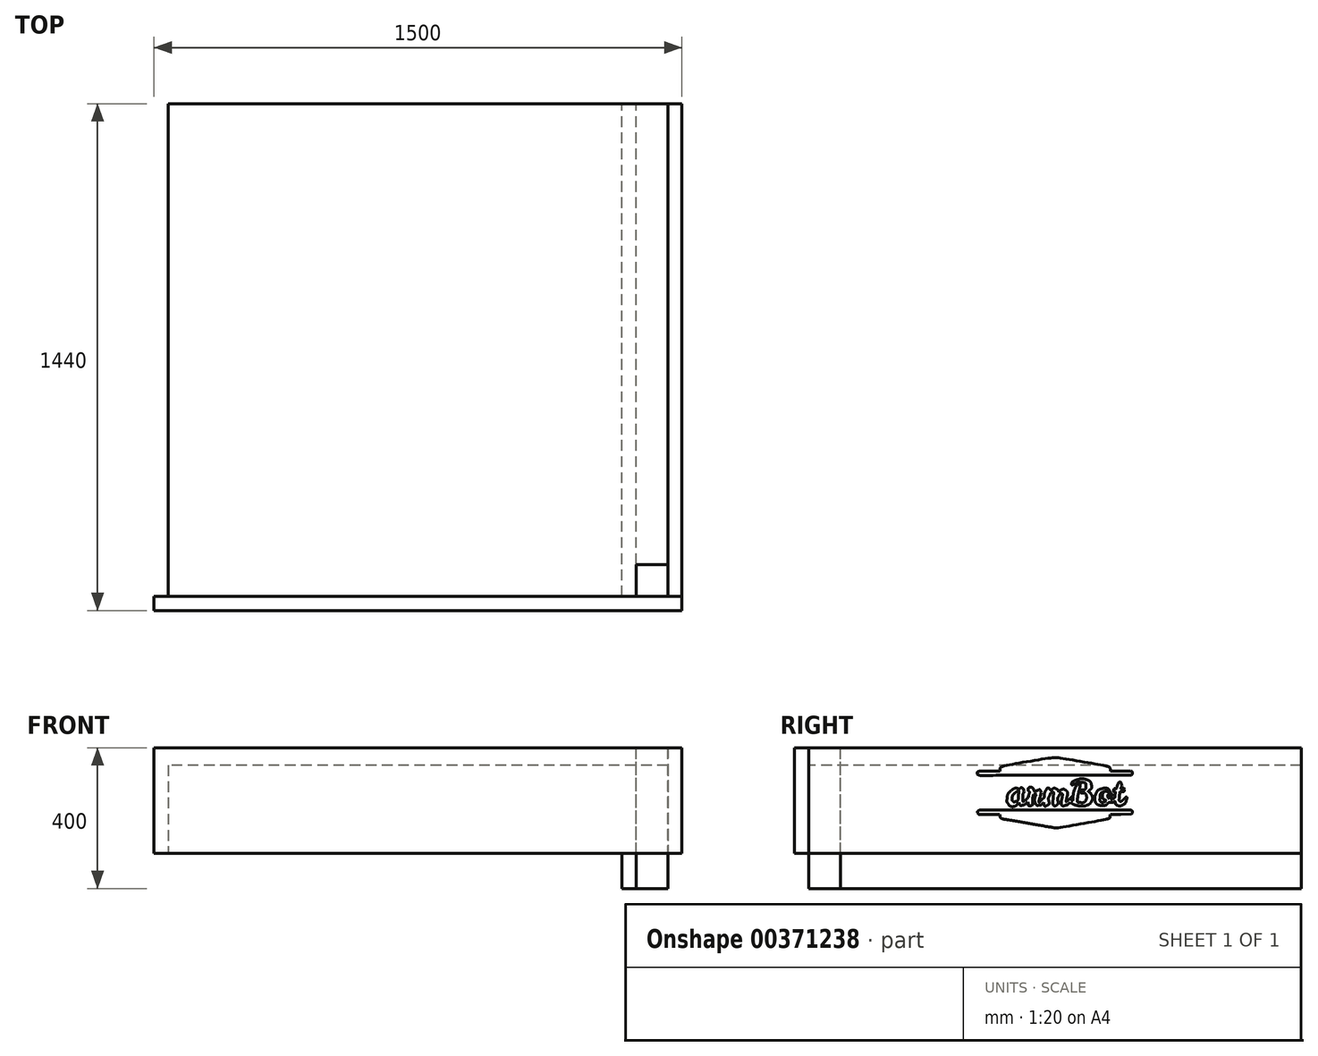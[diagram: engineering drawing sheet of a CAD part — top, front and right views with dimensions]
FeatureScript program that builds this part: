
annotation { "Feature Type Name" : "Feature", "Feature Type Description" : "" }
export const myFeature = defineFeature(function(context is Context, id is Id, definition is map)
    precondition{}
    {
        {
            var Q0;
            Q0=qCreatedBy(makeId("Top.planeOp"),FACE);
            var sketch = newSketch(context, id + "F0", { "sketchPlane" : qUnion([Q0])});
            skLineSegment(sketch, "E0.bottom", {"start": v(710, 700) * mm, "end": v(-710, 700) * mm});
            skLineSegment(sketch, "E0.top", {"start": v(710, -700) * mm, "end": v(-710, -700) * mm});
            skLineSegment(sketch, "E0.left", {"start": v(710, 700) * mm, "end": v(710, -700) * mm});
            skLineSegment(sketch, "E0.right", {"start": v(-710, 700) * mm, "end": v(-710, -700) * mm});
            skPoint(sketch, "E0.middle", {"position": v(0, 0) * mm});
            skSolve(sketch);
        }
        {
            var Q0;
            Q0 = qSketchRegion(id + "F0", true);
            extrude(context, id + "F1", {"entities" : qUnion([Q0]), "depth" : 250 * mm});
        }
        {
            var Q0;
            Q0=makeQuery(id+"F1.opExtrude","SWEPT_FACE",FACE,{"disambiguationData":[OSD([sQuery(id+"F0.wireOp",EDGE,"E0.left")])]});
            var sketch = newSketch(context, id + "F2", { "sketchPlane" : qUnion([Q0])});
            skLineSegment(sketch, "E1.bottom", {"start": v(-700, 0) * mm, "end": v(700, 0) * mm});
            skLineSegment(sketch, "E1.top", {"start": v(-700, 300) * mm, "end": v(700, 300) * mm});
            skLineSegment(sketch, "E1.left", {"start": v(-700, 0) * mm, "end": v(-700, 300) * mm});
            skLineSegment(sketch, "E1.right", {"start": v(700, 0) * mm, "end": v(700, 300) * mm});
            skSolve(sketch);
        }
        {
            var Q0;
            Q0=qSketchRegion(id+"F2",true);
            extrude(context, id + "F3", {"entities" : qUnion([Q0]), "depth" : 40 * mm});
        }
        {
            var Q0;
            Q0=makeQuery(id+"F1.opExtrude","SWEPT_FACE",FACE,{"disambiguationData":[OSD([sQuery(id+"F0.wireOp",EDGE,"E0.top")])]});
            var sketch = newSketch(context, id + "F4", { "sketchPlane" : qUnion([Q0])});
            skLineSegment(sketch, "E2.bottom", {"start": v(-750, 300) * mm, "end": v(750, 300) * mm});
            skLineSegment(sketch, "E2.top", {"start": v(-750, 0) * mm, "end": v(750, 0) * mm});
            skLineSegment(sketch, "E2.left", {"start": v(-750, 300) * mm, "end": v(-750, 0) * mm});
            skLineSegment(sketch, "E2.right", {"start": v(750, 300) * mm, "end": v(750, 0) * mm});
            skSolve(sketch);
        }
        {
            var Q0;
            Q0=qSketchRegion(id+"F4",true);
            extrude(context, id + "F5", {"entities" : qUnion([Q0]), "depth" : 40 * mm});
        }
        {
            var Q0;
            Q0=makeQuery(id+"F1.opExtrude","CAP_FACE",FACE,{"disambiguationData":[OSD([sQuery(id+"F0.wireOp",EDGE,"E0.bottom"),sQuery(id+"F0.wireOp",EDGE,"E0.top"),sQuery(id+"F0.wireOp",EDGE,"E0.left"),sQuery(id+"F0.wireOp",EDGE,"E0.right")])],"isStart":false});
            var sketch = newSketch(context, id + "F6", { "sketchPlane" : qUnion([Q0])});
            skFitSpline(sketch, "E3", {"points": [v(-9.76, -247.93) * mm, v(-14.36, -247) * mm, v(-98.7, -232.48) * mm, v(-197.18, -215.67) * mm]});
            skFitSpline(sketch, "E4", {"points": [v(-197.18, -215.67) * mm, v(-303.5, -197.52) * mm, v(-377.79, -184.02) * mm, v(-380.05, -182.43) * mm]});
            skFitSpline(sketch, "E5", {"points": [v(-380.05, -182.43) * mm, v(-386.35, -178.01) * mm, v(-389.22, -172.54) * mm, v(-390.38, -162.7) * mm]});
            skLineSegment(sketch, "E6", {"start": v(-390.38, -162.7) * mm, "end": v(-391.49, -153.38) * mm});
            skLineSegment(sketch, "E7", {"start": v(-391.49, -153.38) * mm, "end": v(-463.29, -153.35) * mm});
            skFitSpline(sketch, "E8", {"points": [v(-463.29, -153.35) * mm, v(-540.74, -153.32) * mm, v(-542.21, -153.15) * mm, v(-546.84, -143.5) * mm]});
            skFitSpline(sketch, "E9", {"points": [v(-546.84, -143.5) * mm, v(-550.32, -136.23) * mm, v(-547.5, -129.03) * mm, v(-539.62, -125.02) * mm]});
            skFitSpline(sketch, "E10", {"points": [v(-539.62, -125.02) * mm, v(-533.58, -121.95) * mm, v(-503.94, -121.77) * mm, v(0.65, -121.77) * mm]});
            skFitSpline(sketch, "E11", {"points": [v(0.65, -121.77) * mm, v(385.66, -121.76) * mm, v(536.18, -122.34) * mm, v(540.43, -123.82) * mm]});
            skFitSpline(sketch, "E12", {"points": [v(540.43, -123.82) * mm, v(543.67, -124.95) * mm, v(547.14, -127.4) * mm, v(548.14, -129.27) * mm]});
            skFitSpline(sketch, "E13", {"points": [v(548.14, -129.27) * mm, v(551.05, -134.7) * mm, v(550.26, -143.3) * mm, v(546.41, -148.06) * mm]});
            skLineSegment(sketch, "E14", {"start": v(546.41, -148.06) * mm, "end": v(542.86, -152.45) * mm});
            skLineSegment(sketch, "E15", {"start": v(542.86, -152.45) * mm, "end": v(467.85, -153.38) * mm});
            skLineSegment(sketch, "E16", {"start": v(467.85, -153.38) * mm, "end": v(392.83, -154.3) * mm});
            skLineSegment(sketch, "E17", {"start": v(392.83, -154.3) * mm, "end": v(392.5, -162.05) * mm});
            skFitSpline(sketch, "E18", {"points": [v(392.5, -162.05) * mm, v(391.99, -173.78) * mm, v(387.68, -180.46) * mm, v(378.46, -183.85) * mm]});
            skFitSpline(sketch, "E19", {"points": [v(378.46, -183.85) * mm, v(371.97, -186.24) * mm, v(2.57, -250.58) * mm, v(-0.47, -249.85) * mm]});
            skFitSpline(sketch, "E20", {"points": [v(-0.47, -249.85) * mm, v(-0.98, -249.73) * mm, v(-5.16, -248.87) * mm, v(-9.76, -247.93) * mm]});
            skLineSegment(sketch, "E21", {"start": v(-9.76, -247.93) * mm, "end": v(-9.76, -247.93) * mm});
            skFitSpline(sketch, "E22", {"points": [v(163.18, -91.34) * mm, v(144.56, -86.99) * mm, v(127.82, -80.58) * mm, v(118.25, -74.15) * mm]});
            skLineSegment(sketch, "E23", {"start": v(118.25, -74.15) * mm, "end": v(108.82, -67.8) * mm});
            skLineSegment(sketch, "E24", {"start": v(108.82, -67.8) * mm, "end": v(101.7, -74.22) * mm});
            skFitSpline(sketch, "E25", {"points": [v(101.7, -74.22) * mm, v(92.92, -82.15) * mm, v(86.06, -85.78) * mm, v(75.22, -88.2) * mm]});
            skFitSpline(sketch, "E26", {"points": [v(75.22, -88.2) * mm, v(52.86, -93.22) * mm, v(44.33, -75.76) * mm, v(50.52, -37.64) * mm]});
            skFitSpline(sketch, "E27", {"points": [v(50.52, -37.64) * mm, v(54.63, -12.34) * mm, v(54.44, -8.7) * mm, v(48.9, -6.17) * mm]});
            skFitSpline(sketch, "E28", {"points": [v(48.9, -6.17) * mm, v(42.7, -3.35) * mm, v(36.64, -7.44) * mm, v(29.87, -18.99) * mm]});
            skFitSpline(sketch, "E29", {"points": [v(29.87, -18.99) * mm, v(21.01, -34.1) * mm, v(18.43, -44.15) * mm, v(20.53, -55.3) * mm]});
            skFitSpline(sketch, "E30", {"points": [v(20.53, -55.3) * mm, v(21.54, -60.66) * mm, v(22.46, -68.35) * mm, v(22.57, -72.38) * mm]});
            skFitSpline(sketch, "E31", {"points": [v(22.57, -72.38) * mm, v(22.76, -78.97) * mm, v(22, -80.26) * mm, v(14.95, -85.23) * mm]});
            skFitSpline(sketch, "E32", {"points": [v(14.95, -85.23) * mm, v(4.39, -92.68) * mm, v(-7.54, -93.24) * mm, v(-11.04, -86.43) * mm]});
            skFitSpline(sketch, "E33", {"points": [v(-11.04, -86.43) * mm, v(-13.95, -80.76) * mm, v(-14.16, -56.28) * mm, v(-11.54, -26.93) * mm]});
            skFitSpline(sketch, "E34", {"points": [v(-11.54, -26.93) * mm, v(-9.2, -0.66) * mm, v(-9.84, 2.83) * mm, v(-17.07, 2.83) * mm]});
            skFitSpline(sketch, "E35", {"points": [v(-17.07, 2.83) * mm, v(-23.9, 2.83) * mm, v(-30.46, -4.7) * mm, v(-38.87, -22.23) * mm]});
            skFitSpline(sketch, "E36", {"points": [v(-38.87, -22.23) * mm, v(-45.93, -36.93) * mm, v(-46.62, -45.33) * mm, v(-42.27, -63.77) * mm]});
            skFitSpline(sketch, "E37", {"points": [v(-42.27, -63.77) * mm, v(-38.91, -78.01) * mm, v(-39.9, -80.3) * mm, v(-52.19, -87) * mm]});
            skFitSpline(sketch, "E38", {"points": [v(-52.19, -87) * mm, v(-68.26, -95.75) * mm, v(-75.2, -92.86) * mm, v(-77.56, -76.43) * mm]});
            skLineSegment(sketch, "E39", {"start": v(-77.56, -76.43) * mm, "end": v(-78.86, -67.36) * mm});
            skLineSegment(sketch, "E40", {"start": v(-78.86, -67.36) * mm, "end": v(-86.62, -74.83) * mm});
            skFitSpline(sketch, "E41", {"points": [v(-86.62, -74.83) * mm, v(-97.05, -84.9) * mm, v(-104.92, -88.54) * mm, v(-116.78, -88.82) * mm]});
            skFitSpline(sketch, "E42", {"points": [v(-116.78, -88.82) * mm, v(-128.34, -89.1) * mm, v(-132.94, -86) * mm, v(-138.3, -74.35) * mm]});
            skFitSpline(sketch, "E43", {"points": [v(-138.3, -74.35) * mm, v(-144.12, -61.65) * mm, v(-141.58, -31.54) * mm, v(-133.32, -15.58) * mm]});
            skLineSegment(sketch, "E44", {"start": v(-133.32, -15.58) * mm, "end": v(-130.44, -10) * mm});
            skLineSegment(sketch, "E45", {"start": v(-130.44, -10) * mm, "end": v(-141.2, -10.56) * mm});
            skLineSegment(sketch, "E46", {"start": v(-141.2, -10.56) * mm, "end": v(-151.94, -11.12) * mm});
            skLineSegment(sketch, "E47", {"start": v(-151.94, -11.12) * mm, "end": v(-155.34, -25.07) * mm});
            skFitSpline(sketch, "E48", {"points": [v(-155.34, -25.07) * mm, v(-157.97, -35.9) * mm, v(-158.52, -43.56) * mm, v(-157.8, -59.34) * mm]});
            skFitSpline(sketch, "E49", {"points": [v(-157.8, -59.34) * mm, v(-157.29, -70.85) * mm, v(-157.67, -81.12) * mm, v(-158.7, -83.03) * mm]});
            skFitSpline(sketch, "E50", {"points": [v(-158.7, -83.03) * mm, v(-161.25, -87.81) * mm, v(-170.24, -92.01) * mm, v(-177.92, -92.01) * mm]});
            skFitSpline(sketch, "E51", {"points": [v(-177.92, -92.01) * mm, v(-186.08, -92.01) * mm, v(-189.42, -87.45) * mm, v(-191.2, -73.87) * mm]});
            skLineSegment(sketch, "E52", {"start": v(-191.2, -73.87) * mm, "end": v(-192.48, -64.09) * mm});
            skLineSegment(sketch, "E53", {"start": v(-192.48, -64.09) * mm, "end": v(-200.42, -71.4) * mm});
            skFitSpline(sketch, "E54", {"points": [v(-200.42, -71.4) * mm, v(-209.89, -80.13) * mm, v(-220.17, -85.65) * mm, v(-231.87, -88.27) * mm]});
            skFitSpline(sketch, "E55", {"points": [v(-231.87, -88.27) * mm, v(-243.7, -90.92) * mm, v(-250.08, -87.49) * mm, v(-254.4, -76.16) * mm]});
            skLineSegment(sketch, "E56", {"start": v(-254.4, -76.16) * mm, "end": v(-257.65, -67.68) * mm});
            skLineSegment(sketch, "E57", {"start": v(-257.65, -67.68) * mm, "end": v(-262.94, -74.1) * mm});
            skFitSpline(sketch, "E58", {"points": [v(-262.94, -74.1) * mm, v(-279.38, -94.04) * mm, v(-316.37, -95.84) * mm, v(-331.85, -77.45) * mm]});
            skFitSpline(sketch, "E59", {"points": [v(-331.85, -77.45) * mm, v(-339.17, -68.75) * mm, v(-341.42, -59.86) * mm, v(-340.14, -44.75) * mm]});
            skFitSpline(sketch, "E60", {"points": [v(-340.14, -44.75) * mm, v(-338.13, -20.94) * mm, v(-329.14, -1.86) * mm, v(-313.1, 12.61) * mm]});
            skFitSpline(sketch, "E61", {"points": [v(-313.1, 12.61) * mm, v(-297.94, 26.32) * mm, v(-276.95, 32.69) * mm, v(-259.7, 28.82) * mm]});
            skFitSpline(sketch, "E62", {"points": [v(-259.7, 28.82) * mm, v(-252.55, 27.22) * mm, v(-250.45, 27.38) * mm, v(-247.85, 29.73) * mm]});
            skFitSpline(sketch, "E63", {"points": [v(-247.85, 29.73) * mm, v(-240.93, 36) * mm, v(-226.99, 30.32) * mm, v(-220.73, 18.7) * mm]});
            skLineSegment(sketch, "E64", {"start": v(-220.73, 18.7) * mm, "end": v(-217.21, 12.17) * mm});
            skLineSegment(sketch, "E65", {"start": v(-217.21, 12.17) * mm, "end": v(-223.2, 0.02) * mm});
            skFitSpline(sketch, "E66", {"points": [v(-223.2, 0.02) * mm, v(-228.92, -11.58) * mm, v(-229.19, -13.1) * mm, v(-229.16, -33.94) * mm]});
            skFitSpline(sketch, "E67", {"points": [v(-229.16, -33.94) * mm, v(-229.13, -57.9) * mm, v(-228.1, -61.48) * mm, v(-221.81, -59.49) * mm]});
            skFitSpline(sketch, "E68", {"points": [v(-221.81, -59.49) * mm, v(-215.07, -57.35) * mm, v(-188.28, -30.28) * mm, v(-188.28, -25.6) * mm]});
            skFitSpline(sketch, "E69", {"points": [v(-188.28, -25.6) * mm, v(-188.28, -23.36) * mm, v(-186.22, -15.85) * mm, v(-183.7, -8.92) * mm]});
            skFitSpline(sketch, "E70", {"points": [v(-183.7, -8.92) * mm, v(-179.26, 3.33) * mm, v(-179.23, 3.78) * mm, v(-182.54, 7.44) * mm]});
            skFitSpline(sketch, "E71", {"points": [v(-182.54, 7.44) * mm, v(-188.48, 13.98) * mm, v(-190.53, 19.67) * mm, v(-189.3, 26.21) * mm]});
            skFitSpline(sketch, "E72", {"points": [v(-189.3, 26.21) * mm, v(-187.82, 34.15) * mm, v(-182.12, 38.16) * mm, v(-172.31, 38.16) * mm]});
            skFitSpline(sketch, "E73", {"points": [v(-172.31, 38.16) * mm, v(-163.16, 38.16) * mm, v(-156.23, 32.34) * mm, v(-150.73, 20.03) * mm]});
            skFitSpline(sketch, "E74", {"points": [v(-150.73, 20.03) * mm, v(-147.7, 13.24) * mm, v(-146.4, 12.12) * mm, v(-141.55, 12.12) * mm]});
            skFitSpline(sketch, "E75", {"points": [v(-141.55, 12.12) * mm, v(-138.45, 12.12) * mm, v(-130.4, 14.33) * mm, v(-123.66, 17.03) * mm]});
            skFitSpline(sketch, "E76", {"points": [v(-123.66, 17.03) * mm, v(-109.3, 22.78) * mm, v(-107.41, 22.17) * mm, v(-101.2, 9.8) * mm]});
            skLineSegment(sketch, "E77", {"start": v(-101.2, 9.8) * mm, "end": v(-96.87, 1.18) * mm});
            skLineSegment(sketch, "E78", {"start": v(-96.87, 1.18) * mm, "end": v(-104.6, -26.95) * mm});
            skFitSpline(sketch, "E79", {"points": [v(-104.6, -26.95) * mm, v(-115.26, -65.72) * mm, v(-113.52, -68.38) * mm, v(-91.12, -47.46) * mm]});
            skLineSegment(sketch, "E80", {"start": v(-91.12, -47.46) * mm, "end": v(-77.26, -34.51) * mm});
            skLineSegment(sketch, "E81", {"start": v(-77.26, -34.51) * mm, "end": v(-76.15, -22.7) * mm});
            skFitSpline(sketch, "E82", {"points": [v(-76.15, -22.7) * mm, v(-74.76, -7.77) * mm, v(-68.68, 10.87) * mm, v(-61.04, 23.61) * mm]});
            skFitSpline(sketch, "E83", {"points": [v(-61.04, 23.61) * mm, v(-56.21, 31.68) * mm, v(-54.07, 33.61) * mm, v(-49.45, 34.07) * mm]});
            skFitSpline(sketch, "E84", {"points": [v(-49.45, 34.07) * mm, v(-44.95, 34.52) * mm, v(-42.63, 33.32) * mm, v(-38.15, 28.2) * mm]});
            skFitSpline(sketch, "E85", {"points": [v(-38.15, 28.2) * mm, v(-35.04, 24.67) * mm, v(-32.16, 20.74) * mm, v(-31.73, 19.46) * mm]});
            skFitSpline(sketch, "E86", {"points": [v(-31.73, 19.46) * mm, v(-31.21, 17.9) * mm, v(-28.37, 19.02) * mm, v(-23, 22.9) * mm]});
            skFitSpline(sketch, "E87", {"points": [v(-23, 22.9) * mm, v(-11.96, 30.9) * mm, v(-1.17, 32.3) * mm, v(9.54, 27.1) * mm]});
            skFitSpline(sketch, "E88", {"points": [v(9.54, 27.1) * mm, v(18.23, 22.9) * mm, v(22.7, 17.7) * mm, v(24.79, 9.4) * mm]});
            skLineSegment(sketch, "E89", {"start": v(24.79, 9.4) * mm, "end": v(26.04, 4.44) * mm});
            skLineSegment(sketch, "E90", {"start": v(26.04, 4.44) * mm, "end": v(30.92, 9.1) * mm});
            skFitSpline(sketch, "E91", {"points": [v(30.92, 9.1) * mm, v(43.6, 21.22) * mm, v(66.06, 25.1) * mm, v(77.8, 17.18) * mm]});
            skFitSpline(sketch, "E92", {"points": [v(77.8, 17.18) * mm, v(81.26, 14.85) * mm, v(85.14, 10.88) * mm, v(86.42, 8.35) * mm]});
            skFitSpline(sketch, "E93", {"points": [v(86.42, 8.35) * mm, v(90.04, 1.18) * mm, v(89.21, -14.95) * mm, v(84.14, -35.88) * mm]});
            skFitSpline(sketch, "E94", {"points": [v(84.14, -35.88) * mm, v(81.59, -46.43) * mm, v(79.5, -56.26) * mm, v(79.5, -57.73) * mm]});
            skFitSpline(sketch, "E95", {"points": [v(79.5, -57.73) * mm, v(79.5, -63.6) * mm, v(86.26, -59.69) * mm, v(100.97, -45.33) * mm]});
            skFitSpline(sketch, "E96", {"points": [v(100.97, -45.33) * mm, v(110.63, -35.9) * mm, v(117.25, -30.77) * mm, v(118.65, -31.64) * mm]});
            skFitSpline(sketch, "E97", {"points": [v(118.65, -31.64) * mm, v(120.17, -32.58) * mm, v(120.56, -36.5) * mm, v(119.89, -43.92) * mm]});
            skFitSpline(sketch, "E98", {"points": [v(119.89, -43.92) * mm, v(118.95, -54.29) * mm, v(119.1, -54.82) * mm, v(123.1, -54.82) * mm]});
            skFitSpline(sketch, "E99", {"points": [v(123.1, -54.82) * mm, v(127.02, -54.82) * mm, v(127.36, -53.84) * mm, v(128.4, -39.48) * mm]});
            skFitSpline(sketch, "E100", {"points": [v(128.4, -39.48) * mm, v(130.72, -7.09) * mm, v(148.03, 43.77) * mm, v(160.6, 55.09) * mm]});
            skFitSpline(sketch, "E101", {"points": [v(160.6, 55.09) * mm, v(178.01, 70.78) * mm, v(179.9, 58.14) * mm, v(168.42, 2.83) * mm]});
            skFitSpline(sketch, "E102", {"points": [v(168.42, 2.83) * mm, v(163.73, -19.8) * mm, v(158.67, -63.5) * mm, v(160.5, -65.68) * mm]});
            skFitSpline(sketch, "E103", {"points": [v(160.5, -65.68) * mm, v(161.76, -67.18) * mm, v(175.96, -69.61) * mm, v(183.63, -69.64) * mm]});
            skFitSpline(sketch, "E104", {"points": [v(183.63, -69.64) * mm, v(200.98, -69.71) * mm, v(215.69, -61.64) * mm, v(220.83, -49.22) * mm]});
            skFitSpline(sketch, "E105", {"points": [v(220.83, -49.22) * mm, v(224.51, -40.34) * mm, v(222.43, -16.02) * mm, v(217.28, -7.68) * mm]});
            skFitSpline(sketch, "E106", {"points": [v(217.28, -7.68) * mm, v(213.13, -0.96) * mm, v(212.95, -0.9) * mm, v(200.63, -0.9) * mm]});
            skFitSpline(sketch, "E107", {"points": [v(200.63, -0.9) * mm, v(187.27, -0.9) * mm, v(181.1, 1.8) * mm, v(179.39, 8.35) * mm]});
            skFitSpline(sketch, "E108", {"points": [v(179.39, 8.35) * mm, v(178.82, 10.5) * mm, v(179.82, 13.89) * mm, v(181.7, 16.2) * mm]});
            skFitSpline(sketch, "E109", {"points": [v(181.7, 16.2) * mm, v(184.4, 19.56) * mm, v(187.56, 20.46) * mm, v(199.63, 21.31) * mm]});
            skFitSpline(sketch, "E110", {"points": [v(199.63, 21.31) * mm, v(213.63, 22.3) * mm, v(214.4, 22.6) * mm, v(217.02, 27.93) * mm]});
            skFitSpline(sketch, "E111", {"points": [v(217.02, 27.93) * mm, v(218.53, 31) * mm, v(219.77, 38.53) * mm, v(219.78, 44.67) * mm]});
            skFitSpline(sketch, "E112", {"points": [v(219.78, 44.67) * mm, v(219.8, 64.17) * mm, v(211.17, 71.67) * mm, v(187.07, 73.1) * mm]});
            skFitSpline(sketch, "E113", {"points": [v(187.07, 73.1) * mm, v(170.05, 74.11) * mm, v(157.7, 71.45) * mm, v(139.99, 62.97) * mm]});
            skFitSpline(sketch, "E114", {"points": [v(139.99, 62.97) * mm, v(124.82, 55.7) * mm, v(118.55, 54.98) * mm, v(118.55, 60.51) * mm]});
            skFitSpline(sketch, "E115", {"points": [v(118.55, 60.51) * mm, v(118.55, 70.5) * mm, v(143.11, 88.38) * mm, v(165.9, 94.95) * mm]});
            skFitSpline(sketch, "E116", {"points": [v(165.9, 94.95) * mm, v(181.16, 99.36) * mm, v(211.58, 97.92) * mm, v(227.33, 92.04) * mm]});
            skFitSpline(sketch, "E117", {"points": [v(227.33, 92.04) * mm, v(241.91, 86.6) * mm, v(254.67, 73.92) * mm, v(257.71, 61.83) * mm]});
            skFitSpline(sketch, "E118", {"points": [v(257.71, 61.83) * mm, v(262.48, 42.9) * mm, v(259.33, 31.38) * mm, v(245.79, 18.17) * mm]});
            skFitSpline(sketch, "E119", {"points": [v(245.79, 18.17) * mm, v(240.28, 12.8) * mm, v(236.48, 8.4) * mm, v(237.34, 8.4) * mm]});
            skFitSpline(sketch, "E120", {"points": [v(237.34, 8.4) * mm, v(241.01, 8.4) * mm, v(256.17, -7.19) * mm, v(259.81, -14.71) * mm]});
            skFitSpline(sketch, "E121", {"points": [v(259.81, -14.71) * mm, v(265.46, -26.39) * mm, v(265.68, -49.04) * mm, v(260.25, -59.68) * mm]});
            skFitSpline(sketch, "E122", {"points": [v(260.25, -59.68) * mm, v(254.38, -71.16) * mm, v(239.5, -83.55) * mm, v(225.92, -88.28) * mm]});
            skFitSpline(sketch, "E123", {"points": [v(225.92, -88.28) * mm, v(211.44, -93.33) * mm, v(178.53, -94.93) * mm, v(163.18, -91.34) * mm]});
            skFitSpline(sketch, "E124", {"points": [v(-281.84, -62.14) * mm, v(-267.85, -56.85) * mm, v(-259.05, -41.8) * mm, v(-258.98, -23.08) * mm]});
            skFitSpline(sketch, "E125", {"points": [v(-258.98, -23.08) * mm, v(-258.96, -16.37) * mm, v(-258.05, -6.04) * mm, v(-256.95, -0.12) * mm]});
            skFitSpline(sketch, "E126", {"points": [v(-256.95, -0.12) * mm, v(-255.86, 5.8) * mm, v(-255.42, 11.09) * mm, v(-255.98, 11.64) * mm]});
            skFitSpline(sketch, "E127", {"points": [v(-255.98, 11.64) * mm, v(-257.93, 13.6) * mm, v(-273.99, 6.15) * mm, v(-282.7, -0.75) * mm]});
            skFitSpline(sketch, "E128", {"points": [v(-282.7, -0.75) * mm, v(-295.24, -10.66) * mm, v(-302.1, -24.16) * mm, v(-303.18, -41.06) * mm]});
            skFitSpline(sketch, "E129", {"points": [v(-303.18, -41.06) * mm, v(-303.98, -53.62) * mm, v(-303.72, -54.84) * mm, v(-299.24, -59.32) * mm]});
            skFitSpline(sketch, "E130", {"points": [v(-299.24, -59.32) * mm, v(-294.03, -64.53) * mm, v(-289.93, -65.2) * mm, v(-281.84, -62.14) * mm]});
            skFitSpline(sketch, "E131", {"points": [v(-459.3, -89.94) * mm, v(-464.48, -84.62) * mm, v(-460.7, -35.47) * mm, v(-453.32, -12.23) * mm]});
            skFitSpline(sketch, "E132", {"points": [v(-453.32, -12.23) * mm, v(-452.15, -8.52) * mm, v(-452.73, -8.33) * mm, v(-465.23, -8.33) * mm]});
            skFitSpline(sketch, "E133", {"points": [v(-465.23, -8.33) * mm, v(-476.68, -8.33) * mm, v(-478.37, -7.9) * mm, v(-478.37, -4.96) * mm]});
            skFitSpline(sketch, "E134", {"points": [v(-478.37, -4.96) * mm, v(-478.37, 0.26) * mm, v(-468.99, 8.03) * mm, v(-457.1, 12.63) * mm]});
            skLineSegment(sketch, "E135", {"start": v(-457.1, 12.63) * mm, "end": v(-446.32, 16.8) * mm});
            skLineSegment(sketch, "E136", {"start": v(-446.32, 16.8) * mm, "end": v(-438.43, 39.1) * mm});
            skFitSpline(sketch, "E137", {"points": [v(-438.43, 39.1) * mm, v(-434.08, 51.37) * mm, v(-429.87, 62.96) * mm, v(-429.07, 64.87) * mm]});
            skFitSpline(sketch, "E138", {"points": [v(-429.07, 64.87) * mm, v(-427.72, 68.05) * mm, v(-428.28, 68.22) * mm, v(-435.78, 67) * mm]});
            skFitSpline(sketch, "E139", {"points": [v(-435.78, 67) * mm, v(-447.95, 65.04) * mm, v(-458.5, 59.86) * mm, v(-467.75, 51.34) * mm]});
            skFitSpline(sketch, "E140", {"points": [v(-467.75, 51.34) * mm, v(-479.66, 40.36) * mm, v(-483.95, 41.51) * mm, v(-483.95, 55.7) * mm]});
            skFitSpline(sketch, "E141", {"points": [v(-483.95, 55.7) * mm, v(-483.95, 68.83) * mm, v(-467.73, 83.32) * mm, v(-445.28, 90.26) * mm]});
            skFitSpline(sketch, "E142", {"points": [v(-445.28, 90.26) * mm, v(-427.1, 95.87) * mm, v(-406.05, 97.33) * mm, v(-358.74, 96.25) * mm]});
            skFitSpline(sketch, "E143", {"points": [v(-358.74, 96.25) * mm, v(-311.18, 95.17) * mm, v(-311.95, 95.43) * mm, v(-317.58, 82.22) * mm]});
            skFitSpline(sketch, "E144", {"points": [v(-317.58, 82.22) * mm, v(-323.64, 68.03) * mm, v(-324, 67.91) * mm, v(-360.96, 67.88) * mm]});
            skLineSegment(sketch, "E145", {"start": v(-360.96, 67.88) * mm, "end": v(-393.76, 67.85) * mm});
            skLineSegment(sketch, "E146", {"start": v(-393.76, 67.85) * mm, "end": v(-398.66, 47.9) * mm});
            skFitSpline(sketch, "E147", {"points": [v(-398.66, 47.9) * mm, v(-401.36, 36.91) * mm, v(-403.87, 26.67) * mm, v(-404.24, 25.14) * mm]});
            skFitSpline(sketch, "E148", {"points": [v(-404.24, 25.14) * mm, v(-404.8, 22.8) * mm, v(-401.23, 22.27) * mm, v(-381.74, 21.83) * mm]});
            skFitSpline(sketch, "E149", {"points": [v(-381.74, 21.83) * mm, v(-367.15, 21.5) * mm, v(-358.1, 20.53) * mm, v(-357.28, 19.21) * mm]});
            skFitSpline(sketch, "E150", {"points": [v(-357.28, 19.21) * mm, v(-355.76, 16.75) * mm, v(-359.89, 2.02) * mm, v(-363.24, -2.01) * mm]});
            skFitSpline(sketch, "E151", {"points": [v(-363.24, -2.01) * mm, v(-365.2, -4.38) * mm, v(-369.3, -4.62) * mm, v(-389.06, -3.54) * mm]});
            skLineSegment(sketch, "E152", {"start": v(-389.06, -3.54) * mm, "end": v(-412.56, -2.27) * mm});
            skLineSegment(sketch, "E153", {"start": v(-412.56, -2.27) * mm, "end": v(-416.52, -18.78) * mm});
            skFitSpline(sketch, "E154", {"points": [v(-416.52, -18.78) * mm, v(-421.04, -37.64) * mm, v(-423.77, -53.93) * mm, v(-425.45, -72.08) * mm]});
            skFitSpline(sketch, "E155", {"points": [v(-425.45, -72.08) * mm, v(-426.44, -82.86) * mm, v(-427.3, -85.14) * mm, v(-431.33, -87.78) * mm]});
            skFitSpline(sketch, "E156", {"points": [v(-431.33, -87.78) * mm, v(-437.41, -91.77) * mm, v(-456.13, -93.2) * mm, v(-459.3, -89.94) * mm]});
            skFitSpline(sketch, "E157", {"points": [v(317.5, -88.5) * mm, v(302.9, -83.79) * mm, v(289.51, -71.3) * mm, v(285.81, -58.96) * mm]});
            skFitSpline(sketch, "E158", {"points": [v(285.81, -58.96) * mm, v(282.17, -46.8) * mm, v(284.25, -22.14) * mm, v(289.96, -9.87) * mm]});
            skFitSpline(sketch, "E159", {"points": [v(289.96, -9.87) * mm, v(299.26, 10.12) * mm, v(316.09, 24.32) * mm, v(335.9, 28.9) * mm]});
            skFitSpline(sketch, "E160", {"points": [v(335.9, 28.9) * mm, v(354.07, 33.1) * mm, v(378.44, 28.13) * mm, v(386.33, 18.63) * mm]});
            skFitSpline(sketch, "E161", {"points": [v(386.33, 18.63) * mm, v(390.02, 14.18) * mm, v(386.8, 12.82) * mm, v(369.86, 11.65) * mm]});
            skFitSpline(sketch, "E162", {"points": [v(369.86, 11.65) * mm, v(362, 11.12) * mm, v(352.6, 9.43) * mm, v(348.96, 7.91) * mm]});
            skFitSpline(sketch, "E163", {"points": [v(348.96, 7.91) * mm, v(331.95, 0.8) * mm, v(320.77, -16.17) * mm, v(320.52, -35.3) * mm]});
            skFitSpline(sketch, "E164", {"points": [v(320.52, -35.3) * mm, v(320.22, -57.93) * mm, v(334.52, -68.41) * mm, v(357.15, -62.13) * mm]});
            skLineSegment(sketch, "E165", {"start": v(357.15, -62.13) * mm, "end": v(364.23, -60.16) * mm});
            skLineSegment(sketch, "E166", {"start": v(364.23, -60.16) * mm, "end": v(357.84, -53.09) * mm});
            skFitSpline(sketch, "E167", {"points": [v(357.84, -53.09) * mm, v(336.45, -29.41) * mm, v(349.03, 6.55) * mm, v(378.7, 6.55) * mm]});
            skFitSpline(sketch, "E168", {"points": [v(378.7, 6.55) * mm, v(389.23, 6.55) * mm, v(395.06, 3.8) * mm, v(399.43, -3.17) * mm]});
            skFitSpline(sketch, "E169", {"points": [v(399.43, -3.17) * mm, v(402.65, -8.3) * mm, v(403.12, -11.47) * mm, v(402.44, -23.2) * mm]});
            skFitSpline(sketch, "E170", {"points": [v(402.44, -23.2) * mm, v(402, -30.88) * mm, v(401.02, -39.04) * mm, v(400.27, -41.34) * mm]});
            skFitSpline(sketch, "E171", {"points": [v(400.27, -41.34) * mm, v(398.58, -46.51) * mm, v(402.33, -46.92) * mm, v(411.06, -42.52) * mm]});
            skFitSpline(sketch, "E172", {"points": [v(411.06, -42.52) * mm, v(421.31, -37.33) * mm, v(425.37, -32.45) * mm, v(425.44, -25.2) * mm]});
            skFitSpline(sketch, "E173", {"points": [v(425.44, -25.2) * mm, v(425.48, -21.55) * mm, v(426.6, -12.92) * mm, v(427.94, -6.02) * mm]});
            skFitSpline(sketch, "E174", {"points": [v(427.94, -6.02) * mm, v(429.27, 0.87) * mm, v(429.94, 6.94) * mm, v(429.42, 7.46) * mm]});
            skFitSpline(sketch, "E175", {"points": [v(429.42, 7.46) * mm, v(428.9, 7.98) * mm, v(425.6, 8.4) * mm, v(422.07, 8.4) * mm]});
            skFitSpline(sketch, "E176", {"points": [v(422.07, 8.4) * mm, v(415.71, 8.4) * mm, v(415.67, 8.46) * mm, v(416.93, 15.14) * mm]});
            skFitSpline(sketch, "E177", {"points": [v(416.93, 15.14) * mm, v(418.93, 25.81) * mm, v(421.68, 28.86) * mm, v(429.3, 28.86) * mm]});
            skFitSpline(sketch, "E178", {"points": [v(429.3, 28.86) * mm, v(435.8, 28.86) * mm, v(436.17, 29.23) * mm, v(439.97, 39.55) * mm]});
            skFitSpline(sketch, "E179", {"points": [v(439.97, 39.55) * mm, v(450.84, 69.05) * mm, v(465.01, 75.94) * mm, v(473.83, 56) * mm]});
            skLineSegment(sketch, "E180", {"start": v(473.83, 56) * mm, "end": v(477.45, 47.84) * mm});
            skLineSegment(sketch, "E181", {"start": v(477.45, 47.84) * mm, "end": v(472.82, 39.75) * mm});
            skFitSpline(sketch, "E182", {"points": [v(472.82, 39.75) * mm, v(470.27, 35.3) * mm, v(468.18, 31.02) * mm, v(468.17, 30.25) * mm]});
            skFitSpline(sketch, "E183", {"points": [v(468.17, 30.25) * mm, v(468.15, 29.49) * mm, v(474, 28.86) * mm, v(481.16, 28.86) * mm]});
            skFitSpline(sketch, "E184", {"points": [v(481.16, 28.86) * mm, v(493.59, 28.86) * mm, v(494.18, 28.66) * mm, v(494.18, 24.49) * mm]});
            skFitSpline(sketch, "E185", {"points": [v(494.18, 24.49) * mm, v(494.18, 22.08) * mm, v(493.26, 17.48) * mm, v(492.14, 14.26) * mm]});
            skFitSpline(sketch, "E186", {"points": [v(492.14, 14.26) * mm, v(490.1, 8.41) * mm, v(490.07, 8.4) * mm, v(476.53, 8.4) * mm]});
            skFitSpline(sketch, "E187", {"points": [v(476.53, 8.4) * mm, v(466.58, 8.4) * mm, v(462.7, 7.7) * mm, v(461.96, 5.79) * mm]});
            skFitSpline(sketch, "E188", {"points": [v(461.96, 5.79) * mm, v(461.4, 4.35) * mm, v(459.93, -6.74) * mm, v(458.69, -18.85) * mm]});
            skFitSpline(sketch, "E189", {"points": [v(458.69, -18.85) * mm, v(456.19, -43.13) * mm, v(457.42, -58.1) * mm, v(462.05, -59.89) * mm]});
            skFitSpline(sketch, "E190", {"points": [v(462.05, -59.89) * mm, v(466.54, -61.6) * mm, v(480.7, -53.25) * mm, v(493.44, -41.34) * mm]});
            skFitSpline(sketch, "E191", {"points": [v(493.44, -41.34) * mm, v(499.73, -35.46) * mm, v(505.73, -30.65) * mm, v(506.77, -30.65) * mm]});
            skFitSpline(sketch, "E192", {"points": [v(506.77, -30.65) * mm, v(510.1, -30.65) * mm, v(511.02, -39.58) * mm, v(508.46, -47.01) * mm]});
            skFitSpline(sketch, "E193", {"points": [v(508.46, -47.01) * mm, v(500.27, -70.78) * mm, v(464.23, -93.67) * mm, v(443.63, -88.18) * mm]});
            skFitSpline(sketch, "E194", {"points": [v(443.63, -88.18) * mm, v(436.32, -86.23) * mm, v(430.49, -78.96) * mm, v(428.05, -68.77) * mm]});
            skFitSpline(sketch, "E195", {"points": [v(428.05, -68.77) * mm, v(426, -60.18) * mm, v(425.55, -59.99) * mm, v(418.25, -64.52) * mm]});
            skFitSpline(sketch, "E196", {"points": [v(418.25, -64.52) * mm, v(412.67, -68) * mm, v(408.97, -68.73) * mm, v(397.88, -68.57) * mm]});
            skFitSpline(sketch, "E197", {"points": [v(397.88, -68.57) * mm, v(384.98, -68.4) * mm, v(384.01, -68.68) * mm, v(377.5, -74.64) * mm]});
            skFitSpline(sketch, "E198", {"points": [v(377.5, -74.64) * mm, v(365.8, -85.37) * mm, v(355.8, -89.15) * mm, v(337.98, -89.6) * mm]});
            skFitSpline(sketch, "E199", {"points": [v(337.98, -89.6) * mm, v(329.28, -89.82) * mm, v(320.07, -89.33) * mm, v(317.5, -88.5) * mm]});
            skFitSpline(sketch, "E200", {"points": [v(385.7, -25.43) * mm, v(386.64, -17.46) * mm, v(386.3, -15.64) * mm, v(383.66, -14.63) * mm]});
            skFitSpline(sketch, "E201", {"points": [v(383.66, -14.63) * mm, v(379.08, -12.87) * mm, v(376.38, -16.52) * mm, v(376.67, -24.09) * mm]});
            skFitSpline(sketch, "E202", {"points": [v(376.67, -24.09) * mm, v(376.97, -32.15) * mm, v(380.4, -39.18) * mm, v(382.83, -36.75) * mm]});
            skFitSpline(sketch, "E203", {"points": [v(382.83, -36.75) * mm, v(383.78, -35.8) * mm, v(385.07, -30.7) * mm, v(385.7, -25.43) * mm]});
            skFitSpline(sketch, "E204", {"points": [v(-539.73, 126.1) * mm, v(-551.06, 131.84) * mm, v(-551, 146.27) * mm, v(-539.62, 152.05) * mm]});
            skFitSpline(sketch, "E205", {"points": [v(-539.62, 152.05) * mm, v(-533.86, 154.98) * mm, v(-526.13, 155.3) * mm, v(-462.1, 155.3) * mm]});
            skLineSegment(sketch, "E206", {"start": v(-462.1, 155.3) * mm, "end": v(-390.97, 155.3) * mm});
            skLineSegment(sketch, "E207", {"start": v(-390.97, 155.3) * mm, "end": v(-390.97, 160.85) * mm});
            skFitSpline(sketch, "E208", {"points": [v(-390.97, 160.85) * mm, v(-390.97, 170.05) * mm, v(-385.48, 181.2) * mm, v(-379.4, 184.35) * mm]});
            skFitSpline(sketch, "E209", {"points": [v(-379.4, 184.35) * mm, v(-373.17, 187.57) * mm, v(-10.28, 250.15) * mm, v(2.18, 250.15) * mm]});
            skFitSpline(sketch, "E210", {"points": [v(2.18, 250.15) * mm, v(10.33, 250.15) * mm, v(362.94, 190.41) * mm, v(375.5, 186.9) * mm]});
            skFitSpline(sketch, "E211", {"points": [v(375.5, 186.9) * mm, v(384.93, 184.27) * mm, v(391.52, 175.86) * mm, v(393.02, 164.53) * mm]});
            skLineSegment(sketch, "E212", {"start": v(393.02, 164.53) * mm, "end": v(394.24, 155.3) * mm});
            skLineSegment(sketch, "E213", {"start": v(394.24, 155.3) * mm, "end": v(464.39, 155.3) * mm});
            skFitSpline(sketch, "E214", {"points": [v(464.39, 155.3) * mm, v(536.67, 155.3) * mm, v(544.5, 154.6) * mm, v(548.14, 147.8) * mm]});
            skFitSpline(sketch, "E215", {"points": [v(548.14, 147.8) * mm, v(551.05, 142.36) * mm, v(550.26, 133.77) * mm, v(546.41, 129.02) * mm]});
            skLineSegment(sketch, "E216", {"start": v(546.41, 129.02) * mm, "end": v(542.86, 124.63) * mm});
            skLineSegment(sketch, "E217", {"start": v(542.86, 124.63) * mm, "end": v(3.88, 124.18) * mm});
            skFitSpline(sketch, "E218", {"points": [v(3.88, 124.18) * mm, v(-428.24, 123.83) * mm, v(-536, 124.2) * mm, v(-539.73, 126.1) * mm]});
            skLineSegment(sketch, "E219", {"start": v(-539.73, 126.1) * mm, "end": v(-539.73, 126.1) * mm});
            skSolve(sketch);
        }
        {
            var Q0;
            Q0=makeQuery(id+"F3.opExtrude","CAP_FACE",FACE,{"disambiguationData":[OSD([sQuery(id+"F2.wireOp",EDGE,"E1.bottom"),sQuery(id+"F2.wireOp",EDGE,"E1.top"),sQuery(id+"F2.wireOp",EDGE,"E1.left"),sQuery(id+"F2.wireOp",EDGE,"E1.right")])],"isStart":false});
            var sketch = newSketch(context, id + "F7", { "sketchPlane" : qUnion([Q0])});
            skFitSpline(sketch, "E220", {"points": [v(-4.02, 72.8) * mm, v(-5.86, 73.18) * mm, v(-39.6, 78.99) * mm, v(-78.98, 85.71) * mm]});
            skFitSpline(sketch, "E221", {"points": [v(-78.98, 85.71) * mm, v(-121.51, 92.97) * mm, v(-151.23, 98.37) * mm, v(-152.13, 99) * mm]});
            skFitSpline(sketch, "E222", {"points": [v(-152.13, 99) * mm, v(-154.65, 100.77) * mm, v(-155.8, 102.96) * mm, v(-156.27, 106.9) * mm]});
            skLineSegment(sketch, "E223", {"start": v(-156.27, 106.9) * mm, "end": v(-156.7, 110.63) * mm});
            skLineSegment(sketch, "E224", {"start": v(-156.7, 110.63) * mm, "end": v(-185.43, 110.64) * mm});
            skFitSpline(sketch, "E225", {"points": [v(-185.43, 110.64) * mm, v(-216.4, 110.65) * mm, v(-217, 110.72) * mm, v(-218.85, 114.58) * mm]});
            skFitSpline(sketch, "E226", {"points": [v(-218.85, 114.58) * mm, v(-220.24, 117.49) * mm, v(-219.12, 120.37) * mm, v(-215.96, 121.97) * mm]});
            skFitSpline(sketch, "E227", {"points": [v(-215.96, 121.97) * mm, v(-213.54, 123.2) * mm, v(-201.69, 123.27) * mm, v(0.15, 123.27) * mm]});
            skFitSpline(sketch, "E228", {"points": [v(0.15, 123.27) * mm, v(154.15, 123.27) * mm, v(214.36, 123.04) * mm, v(216.06, 122.45) * mm]});
            skFitSpline(sketch, "E229", {"points": [v(216.06, 122.45) * mm, v(217.36, 122) * mm, v(218.75, 121.02) * mm, v(219.15, 120.27) * mm]});
            skFitSpline(sketch, "E230", {"points": [v(219.15, 120.27) * mm, v(220.3, 118.1) * mm, v(220, 114.66) * mm, v(218.45, 112.76) * mm]});
            skLineSegment(sketch, "E231", {"start": v(218.45, 112.76) * mm, "end": v(217.03, 111) * mm});
            skLineSegment(sketch, "E232", {"start": v(217.03, 111) * mm, "end": v(187.03, 110.63) * mm});
            skLineSegment(sketch, "E233", {"start": v(187.03, 110.63) * mm, "end": v(157.02, 110.26) * mm});
            skLineSegment(sketch, "E234", {"start": v(157.02, 110.26) * mm, "end": v(156.89, 107.16) * mm});
            skFitSpline(sketch, "E235", {"points": [v(156.89, 107.16) * mm, v(156.68, 102.47) * mm, v(154.96, 99.8) * mm, v(151.27, 98.44) * mm]});
            skFitSpline(sketch, "E236", {"points": [v(151.27, 98.44) * mm, v(148.68, 97.48) * mm, v(0.92, 71.75) * mm, v(-0.3, 72.04) * mm]});
            skFitSpline(sketch, "E237", {"points": [v(-0.3, 72.04) * mm, v(-0.5, 72.09) * mm, v(-2.18, 72.43) * mm, v(-4.02, 72.8) * mm]});
            skLineSegment(sketch, "E238", {"start": v(-4.02, 72.8) * mm, "end": v(-4.02, 72.8) * mm});
            skFitSpline(sketch, "E239", {"points": [v(65.16, 135.44) * mm, v(57.71, 137.18) * mm, v(51.02, 139.75) * mm, v(47.2, 142.32) * mm]});
            skLineSegment(sketch, "E240", {"start": v(47.2, 142.32) * mm, "end": v(43.41, 144.86) * mm});
            skLineSegment(sketch, "E241", {"start": v(43.41, 144.86) * mm, "end": v(40.57, 142.3) * mm});
            skFitSpline(sketch, "E242", {"points": [v(40.57, 142.3) * mm, v(37.06, 139.12) * mm, v(34.31, 137.67) * mm, v(29.98, 136.7) * mm]});
            skFitSpline(sketch, "E243", {"points": [v(29.98, 136.7) * mm, v(21.03, 134.7) * mm, v(17.62, 141.67) * mm, v(20.1, 156.92) * mm]});
            skFitSpline(sketch, "E244", {"points": [v(20.1, 156.92) * mm, v(21.74, 167.04) * mm, v(21.67, 168.5) * mm, v(19.44, 169.51) * mm]});
            skFitSpline(sketch, "E245", {"points": [v(19.44, 169.51) * mm, v(16.97, 170.64) * mm, v(14.54, 169) * mm, v(11.84, 164.39) * mm]});
            skFitSpline(sketch, "E246", {"points": [v(11.84, 164.39) * mm, v(8.3, 158.34) * mm, v(7.26, 154.32) * mm, v(8.1, 149.86) * mm]});
            skFitSpline(sketch, "E247", {"points": [v(8.1, 149.86) * mm, v(8.5, 147.71) * mm, v(8.87, 144.64) * mm, v(8.92, 143.03) * mm]});
            skFitSpline(sketch, "E248", {"points": [v(8.92, 143.03) * mm, v(9, 140.4) * mm, v(8.69, 139.88) * mm, v(5.87, 137.89) * mm]});
            skFitSpline(sketch, "E249", {"points": [v(5.87, 137.89) * mm, v(1.64, 134.9) * mm, v(-3.13, 134.68) * mm, v(-4.53, 137.4) * mm]});
            skFitSpline(sketch, "E250", {"points": [v(-4.53, 137.4) * mm, v(-5.7, 139.68) * mm, v(-5.78, 149.47) * mm, v(-4.73, 161.2) * mm]});
            skFitSpline(sketch, "E251", {"points": [v(-4.73, 161.2) * mm, v(-3.79, 171.71) * mm, v(-4.05, 173.1) * mm, v(-6.94, 173.1) * mm]});
            skFitSpline(sketch, "E252", {"points": [v(-6.94, 173.1) * mm, v(-9.67, 173.1) * mm, v(-12.3, 170.1) * mm, v(-15.66, 163.09) * mm]});
            skFitSpline(sketch, "E253", {"points": [v(-15.66, 163.09) * mm, v(-18.48, 157.2) * mm, v(-18.76, 153.85) * mm, v(-17.02, 146.47) * mm]});
            skFitSpline(sketch, "E254", {"points": [v(-17.02, 146.47) * mm, v(-15.68, 140.78) * mm, v(-16.07, 139.86) * mm, v(-20.99, 137.18) * mm]});
            skFitSpline(sketch, "E255", {"points": [v(-20.99, 137.18) * mm, v(-27.42, 133.68) * mm, v(-30.19, 134.83) * mm, v(-31.13, 141.4) * mm]});
            skLineSegment(sketch, "E256", {"start": v(-31.13, 141.4) * mm, "end": v(-31.66, 145.04) * mm});
            skLineSegment(sketch, "E257", {"start": v(-31.66, 145.04) * mm, "end": v(-34.76, 142.05) * mm});
            skFitSpline(sketch, "E258", {"points": [v(-34.76, 142.05) * mm, v(-38.93, 138.02) * mm, v(-42.08, 136.56) * mm, v(-46.82, 136.45) * mm]});
            skFitSpline(sketch, "E259", {"points": [v(-46.82, 136.45) * mm, v(-51.45, 136.34) * mm, v(-53.29, 137.58) * mm, v(-55.43, 142.24) * mm]});
            skFitSpline(sketch, "E260", {"points": [v(-55.43, 142.24) * mm, v(-57.76, 147.32) * mm, v(-56.74, 159.36) * mm, v(-53.44, 165.75) * mm]});
            skLineSegment(sketch, "E261", {"start": v(-53.44, 165.75) * mm, "end": v(-52.29, 167.98) * mm});
            skLineSegment(sketch, "E262", {"start": v(-52.29, 167.98) * mm, "end": v(-56.59, 167.76) * mm});
            skLineSegment(sketch, "E263", {"start": v(-56.59, 167.76) * mm, "end": v(-60.89, 167.53) * mm});
            skLineSegment(sketch, "E264", {"start": v(-60.89, 167.53) * mm, "end": v(-62.25, 161.95) * mm});
            skFitSpline(sketch, "E265", {"points": [v(-62.25, 161.95) * mm, v(-63.3, 157.62) * mm, v(-63.52, 154.56) * mm, v(-63.24, 148.25) * mm]});
            skFitSpline(sketch, "E266", {"points": [v(-63.24, 148.25) * mm, v(-63.03, 143.64) * mm, v(-63.18, 139.53) * mm, v(-63.59, 138.77) * mm]});
            skFitSpline(sketch, "E267", {"points": [v(-63.59, 138.77) * mm, v(-64.61, 136.85) * mm, v(-68.2, 135.17) * mm, v(-71.28, 135.17) * mm]});
            skFitSpline(sketch, "E268", {"points": [v(-71.28, 135.17) * mm, v(-74.54, 135.17) * mm, v(-75.88, 137) * mm, v(-76.6, 142.43) * mm]});
            skLineSegment(sketch, "E269", {"start": v(-76.6, 142.43) * mm, "end": v(-77.1, 146.34) * mm});
            skLineSegment(sketch, "E270", {"start": v(-77.1, 146.34) * mm, "end": v(-80.28, 143.42) * mm});
            skFitSpline(sketch, "E271", {"points": [v(-80.28, 143.42) * mm, v(-84.07, 139.93) * mm, v(-88.18, 137.72) * mm, v(-92.86, 136.67) * mm]});
            skFitSpline(sketch, "E272", {"points": [v(-92.86, 136.67) * mm, v(-97.59, 135.61) * mm, v(-100.15, 136.99) * mm, v(-101.87, 141.51) * mm]});
            skLineSegment(sketch, "E273", {"start": v(-101.87, 141.51) * mm, "end": v(-103.17, 144.9) * mm});
            skLineSegment(sketch, "E274", {"start": v(-103.17, 144.9) * mm, "end": v(-105.29, 142.34) * mm});
            skFitSpline(sketch, "E275", {"points": [v(-105.29, 142.34) * mm, v(-111.87, 134.36) * mm, v(-126.66, 133.64) * mm, v(-132.85, 141) * mm]});
            skFitSpline(sketch, "E276", {"points": [v(-132.85, 141) * mm, v(-135.78, 144.48) * mm, v(-136.68, 148.03) * mm, v(-136.17, 154.08) * mm]});
            skFitSpline(sketch, "E277", {"points": [v(-136.17, 154.08) * mm, v(-135.36, 163.6) * mm, v(-131.77, 171.23) * mm, v(-125.36, 177.03) * mm]});
            skFitSpline(sketch, "E278", {"points": [v(-125.36, 177.03) * mm, v(-119.29, 182.5) * mm, v(-110.9, 185.05) * mm, v(-104, 183.5) * mm]});
            skFitSpline(sketch, "E279", {"points": [v(-104, 183.5) * mm, v(-101.13, 182.87) * mm, v(-100.3, 182.93) * mm, v(-99.25, 183.87) * mm]});
            skFitSpline(sketch, "E280", {"points": [v(-99.25, 183.87) * mm, v(-96.48, 186.38) * mm, v(-90.9, 184.1) * mm, v(-88.4, 179.46) * mm]});
            skLineSegment(sketch, "E281", {"start": v(-88.4, 179.46) * mm, "end": v(-87, 176.85) * mm});
            skLineSegment(sketch, "E282", {"start": v(-87, 176.85) * mm, "end": v(-89.4, 171.99) * mm});
            skFitSpline(sketch, "E283", {"points": [v(-89.4, 171.99) * mm, v(-91.68, 167.35) * mm, v(-91.79, 166.74) * mm, v(-91.78, 158.4) * mm]});
            skFitSpline(sketch, "E284", {"points": [v(-91.78, 158.4) * mm, v(-91.76, 148.82) * mm, v(-91.35, 147.39) * mm, v(-88.84, 148.18) * mm]});
            skFitSpline(sketch, "E285", {"points": [v(-88.84, 148.18) * mm, v(-86.14, 149.04) * mm, v(-75.42, 159.87) * mm, v(-75.42, 161.74) * mm]});
            skFitSpline(sketch, "E286", {"points": [v(-75.42, 161.74) * mm, v(-75.42, 162.64) * mm, v(-74.6, 165.64) * mm, v(-73.6, 168.41) * mm]});
            skFitSpline(sketch, "E287", {"points": [v(-73.6, 168.41) * mm, v(-71.82, 173.31) * mm, v(-71.8, 173.5) * mm, v(-73.13, 174.95) * mm]});
            skFitSpline(sketch, "E288", {"points": [v(-73.13, 174.95) * mm, v(-75.5, 177.57) * mm, v(-76.32, 179.85) * mm, v(-75.83, 182.46) * mm]});
            skFitSpline(sketch, "E289", {"points": [v(-75.83, 182.46) * mm, v(-75.24, 185.64) * mm, v(-72.96, 187.24) * mm, v(-69.04, 187.24) * mm]});
            skFitSpline(sketch, "E290", {"points": [v(-69.04, 187.24) * mm, v(-65.37, 187.24) * mm, v(-62.6, 184.92) * mm, v(-60.4, 180) * mm]});
            skFitSpline(sketch, "E291", {"points": [v(-60.4, 180) * mm, v(-59.19, 177.28) * mm, v(-58.67, 176.83) * mm, v(-56.73, 176.83) * mm]});
            skFitSpline(sketch, "E292", {"points": [v(-56.73, 176.83) * mm, v(-55.5, 176.83) * mm, v(-52.27, 177.71) * mm, v(-49.58, 178.8) * mm]});
            skFitSpline(sketch, "E293", {"points": [v(-49.58, 178.8) * mm, v(-43.83, 181.09) * mm, v(-43.08, 180.85) * mm, v(-40.6, 175.9) * mm]});
            skLineSegment(sketch, "E294", {"start": v(-40.6, 175.9) * mm, "end": v(-38.86, 172.45) * mm});
            skLineSegment(sketch, "E295", {"start": v(-38.86, 172.45) * mm, "end": v(-41.95, 161.2) * mm});
            skFitSpline(sketch, "E296", {"points": [v(-41.95, 161.2) * mm, v(-46.22, 145.7) * mm, v(-45.52, 144.63) * mm, v(-36.56, 153) * mm]});
            skLineSegment(sketch, "E297", {"start": v(-36.56, 153) * mm, "end": v(-31.01, 158.17) * mm});
            skLineSegment(sketch, "E298", {"start": v(-31.01, 158.17) * mm, "end": v(-30.57, 162.9) * mm});
            skFitSpline(sketch, "E299", {"points": [v(-30.57, 162.9) * mm, v(-30.02, 168.87) * mm, v(-27.58, 176.33) * mm, v(-24.53, 181.43) * mm]});
            skFitSpline(sketch, "E300", {"points": [v(-24.53, 181.43) * mm, v(-22.6, 184.65) * mm, v(-21.74, 185.42) * mm, v(-19.9, 185.6) * mm]});
            skFitSpline(sketch, "E301", {"points": [v(-19.9, 185.6) * mm, v(-18.1, 185.79) * mm, v(-17.17, 185.3) * mm, v(-15.37, 183.26) * mm]});
            skFitSpline(sketch, "E302", {"points": [v(-15.37, 183.26) * mm, v(-14.13, 181.85) * mm, v(-12.97, 180.27) * mm, v(-12.8, 179.76) * mm]});
            skFitSpline(sketch, "E303", {"points": [v(-12.8, 179.76) * mm, v(-12.6, 179.14) * mm, v(-11.46, 179.59) * mm, v(-9.31, 181.14) * mm]});
            skFitSpline(sketch, "E304", {"points": [v(-9.31, 181.14) * mm, v(-4.9, 184.34) * mm, v(-0.58, 184.9) * mm, v(3.7, 182.82) * mm]});
            skFitSpline(sketch, "E305", {"points": [v(3.7, 182.82) * mm, v(7.18, 181.14) * mm, v(8.97, 179.06) * mm, v(9.8, 175.74) * mm]});
            skLineSegment(sketch, "E306", {"start": v(9.8, 175.74) * mm, "end": v(10.3, 173.75) * mm});
            skLineSegment(sketch, "E307", {"start": v(10.3, 173.75) * mm, "end": v(12.25, 175.62) * mm});
            skFitSpline(sketch, "E308", {"points": [v(12.25, 175.62) * mm, v(17.33, 180.47) * mm, v(26.31, 182.02) * mm, v(31, 178.85) * mm]});
            skFitSpline(sketch, "E309", {"points": [v(31, 178.85) * mm, v(32.4, 177.92) * mm, v(33.94, 176.33) * mm, v(34.45, 175.32) * mm]});
            skFitSpline(sketch, "E310", {"points": [v(34.45, 175.32) * mm, v(35.9, 172.45) * mm, v(35.57, 166) * mm, v(33.55, 157.63) * mm]});
            skFitSpline(sketch, "E311", {"points": [v(33.55, 157.63) * mm, v(32.52, 153.4) * mm, v(31.69, 149.48) * mm, v(31.69, 148.89) * mm]});
            skFitSpline(sketch, "E312", {"points": [v(31.69, 148.89) * mm, v(31.69, 146.54) * mm, v(34.4, 148.1) * mm, v(40.28, 153.85) * mm]});
            skFitSpline(sketch, "E313", {"points": [v(40.28, 153.85) * mm, v(44.14, 157.62) * mm, v(46.79, 159.67) * mm, v(47.35, 159.33) * mm]});
            skFitSpline(sketch, "E314", {"points": [v(47.35, 159.33) * mm, v(47.95, 158.95) * mm, v(48.11, 157.38) * mm, v(47.84, 154.41) * mm]});
            skFitSpline(sketch, "E315", {"points": [v(47.84, 154.41) * mm, v(47.47, 150.27) * mm, v(47.53, 150.05) * mm, v(49.13, 150.05) * mm]});
            skFitSpline(sketch, "E316", {"points": [v(49.13, 150.05) * mm, v(50.7, 150.05) * mm, v(50.83, 150.44) * mm, v(51.25, 156.19) * mm]});
            skFitSpline(sketch, "E317", {"points": [v(51.25, 156.19) * mm, v(52.17, 169.14) * mm, v(59.1, 189.49) * mm, v(64.13, 194.01) * mm]});
            skFitSpline(sketch, "E318", {"points": [v(64.13, 194.01) * mm, v(71.1, 200.3) * mm, v(71.85, 195.23) * mm, v(67.26, 173.1) * mm]});
            skFitSpline(sketch, "E319", {"points": [v(67.26, 173.1) * mm, v(65.38, 164.06) * mm, v(63.36, 146.58) * mm, v(64.09, 145.7) * mm]});
            skFitSpline(sketch, "E320", {"points": [v(64.09, 145.7) * mm, v(64.6, 145.1) * mm, v(70.27, 144.14) * mm, v(73.34, 144.12) * mm]});
            skFitSpline(sketch, "E321", {"points": [v(73.34, 144.12) * mm, v(80.28, 144.1) * mm, v(86.16, 147.32) * mm, v(88.22, 152.3) * mm]});
            skFitSpline(sketch, "E322", {"points": [v(88.22, 152.3) * mm, v(89.7, 155.84) * mm, v(88.86, 165.57) * mm, v(86.8, 168.9) * mm]});
            skFitSpline(sketch, "E323", {"points": [v(86.8, 168.9) * mm, v(85.14, 171.6) * mm, v(85.07, 171.62) * mm, v(80.14, 171.62) * mm]});
            skFitSpline(sketch, "E324", {"points": [v(80.14, 171.62) * mm, v(74.8, 171.62) * mm, v(72.33, 172.7) * mm, v(71.64, 175.32) * mm]});
            skFitSpline(sketch, "E325", {"points": [v(71.64, 175.32) * mm, v(71.42, 176.18) * mm, v(71.81, 177.53) * mm, v(72.57, 178.46) * mm]});
            skFitSpline(sketch, "E326", {"points": [v(72.57, 178.46) * mm, v(73.65, 179.8) * mm, v(74.91, 180.16) * mm, v(79.74, 180.5) * mm]});
            skFitSpline(sketch, "E327", {"points": [v(79.74, 180.5) * mm, v(85.34, 180.9) * mm, v(85.65, 181.02) * mm, v(86.7, 183.15) * mm]});
            skFitSpline(sketch, "E328", {"points": [v(86.7, 183.15) * mm, v(87.3, 184.38) * mm, v(87.8, 187.4) * mm, v(87.8, 189.85) * mm]});
            skFitSpline(sketch, "E329", {"points": [v(87.8, 189.85) * mm, v(87.81, 197.65) * mm, v(84.36, 200.65) * mm, v(74.71, 201.22) * mm]});
            skFitSpline(sketch, "E330", {"points": [v(74.71, 201.22) * mm, v(67.9, 201.62) * mm, v(62.96, 200.56) * mm, v(55.88, 197.17) * mm]});
            skFitSpline(sketch, "E331", {"points": [v(55.88, 197.17) * mm, v(49.82, 194.26) * mm, v(47.3, 193.97) * mm, v(47.3, 196.18) * mm]});
            skFitSpline(sketch, "E332", {"points": [v(47.3, 196.18) * mm, v(47.3, 200.18) * mm, v(57.13, 207.33) * mm, v(66.24, 209.96) * mm]});
            skFitSpline(sketch, "E333", {"points": [v(66.24, 209.96) * mm, v(72.35, 211.72) * mm, v(84.52, 211.15) * mm, v(90.82, 208.8) * mm]});
            skFitSpline(sketch, "E334", {"points": [v(90.82, 208.8) * mm, v(96.65, 206.62) * mm, v(101.76, 201.55) * mm, v(102.97, 196.71) * mm]});
            skFitSpline(sketch, "E335", {"points": [v(102.97, 196.71) * mm, v(104.88, 189.14) * mm, v(103.62, 184.53) * mm, v(98.2, 179.25) * mm]});
            skFitSpline(sketch, "E336", {"points": [v(98.2, 179.25) * mm, v(96, 177.1) * mm, v(94.48, 175.34) * mm, v(94.82, 175.34) * mm]});
            skFitSpline(sketch, "E337", {"points": [v(94.82, 175.34) * mm, v(96.3, 175.34) * mm, v(102.36, 169.1) * mm, v(103.81, 166.1) * mm]});
            skFitSpline(sketch, "E338", {"points": [v(103.81, 166.1) * mm, v(106.07, 161.42) * mm, v(106.16, 152.36) * mm, v(103.99, 148.1) * mm]});
            skFitSpline(sketch, "E339", {"points": [v(103.99, 148.1) * mm, v(101.64, 143.52) * mm, v(95.7, 138.56) * mm, v(90.26, 136.67) * mm]});
            skFitSpline(sketch, "E340", {"points": [v(90.26, 136.67) * mm, v(84.46, 134.65) * mm, v(71.3, 134) * mm, v(65.16, 135.44) * mm]});
            skFitSpline(sketch, "E341", {"points": [v(-112.85, 147.12) * mm, v(-107.25, 149.24) * mm, v(-103.73, 155.26) * mm, v(-103.7, 162.75) * mm]});
            skFitSpline(sketch, "E342", {"points": [v(-103.7, 162.75) * mm, v(-103.7, 165.43) * mm, v(-103.33, 169.57) * mm, v(-102.9, 171.93) * mm]});
            skFitSpline(sketch, "E343", {"points": [v(-102.9, 171.93) * mm, v(-102.46, 174.3) * mm, v(-102.28, 176.41) * mm, v(-102.5, 176.64) * mm]});
            skFitSpline(sketch, "E344", {"points": [v(-102.5, 176.64) * mm, v(-103.28, 177.42) * mm, v(-109.7, 174.44) * mm, v(-113.2, 171.68) * mm]});
            skFitSpline(sketch, "E345", {"points": [v(-113.2, 171.68) * mm, v(-118.2, 167.72) * mm, v(-120.95, 162.32) * mm, v(-121.38, 155.55) * mm]});
            skFitSpline(sketch, "E346", {"points": [v(-121.38, 155.55) * mm, v(-121.7, 150.53) * mm, v(-121.6, 150.04) * mm, v(-119.8, 148.25) * mm]});
            skFitSpline(sketch, "E347", {"points": [v(-119.8, 148.25) * mm, v(-117.72, 146.17) * mm, v(-116.09, 145.9) * mm, v(-112.85, 147.12) * mm]});
            skFitSpline(sketch, "E348", {"points": [v(-183.84, 136) * mm, v(-185.9, 138.13) * mm, v(-184.4, 157.8) * mm, v(-181.44, 167.09) * mm]});
            skFitSpline(sketch, "E349", {"points": [v(-181.44, 167.09) * mm, v(-180.97, 168.57) * mm, v(-181.2, 168.65) * mm, v(-186.2, 168.65) * mm]});
            skFitSpline(sketch, "E350", {"points": [v(-186.2, 168.65) * mm, v(-190.78, 168.65) * mm, v(-191.46, 168.82) * mm, v(-191.46, 170) * mm]});
            skFitSpline(sketch, "E351", {"points": [v(-191.46, 170) * mm, v(-191.46, 172.08) * mm, v(-187.7, 175.19) * mm, v(-182.96, 177.03) * mm]});
            skLineSegment(sketch, "E352", {"start": v(-182.96, 177.03) * mm, "end": v(-178.64, 178.7) * mm});
            skLineSegment(sketch, "E353", {"start": v(-178.64, 178.7) * mm, "end": v(-175.48, 187.62) * mm});
            skFitSpline(sketch, "E354", {"points": [v(-175.48, 187.62) * mm, v(-173.75, 192.53) * mm, v(-172.06, 197.16) * mm, v(-171.74, 197.93) * mm]});
            skFitSpline(sketch, "E355", {"points": [v(-171.74, 197.93) * mm, v(-171.2, 199.2) * mm, v(-171.42, 199.27) * mm, v(-174.43, 198.78) * mm]});
            skFitSpline(sketch, "E356", {"points": [v(-174.43, 198.78) * mm, v(-179.3, 198) * mm, v(-183.51, 195.92) * mm, v(-187.21, 192.52) * mm]});
            skFitSpline(sketch, "E357", {"points": [v(-187.21, 192.52) * mm, v(-191.98, 188.12) * mm, v(-193.7, 188.58) * mm, v(-193.7, 194.26) * mm]});
            skFitSpline(sketch, "E358", {"points": [v(-193.7, 194.26) * mm, v(-193.7, 199.51) * mm, v(-187.2, 205.3) * mm, v(-178.22, 208.08) * mm]});
            skFitSpline(sketch, "E359", {"points": [v(-178.22, 208.08) * mm, v(-170.95, 210.33) * mm, v(-162.53, 210.91) * mm, v(-143.6, 210.48) * mm]});
            skFitSpline(sketch, "E360", {"points": [v(-143.6, 210.48) * mm, v(-124.58, 210.05) * mm, v(-124.9, 210.15) * mm, v(-127.15, 204.87) * mm]});
            skFitSpline(sketch, "E361", {"points": [v(-127.15, 204.87) * mm, v(-129.57, 199.2) * mm, v(-129.71, 199.15) * mm, v(-144.5, 199.13) * mm]});
            skLineSegment(sketch, "E362", {"start": v(-144.5, 199.13) * mm, "end": v(-157.62, 199.12) * mm});
            skLineSegment(sketch, "E363", {"start": v(-157.62, 199.12) * mm, "end": v(-159.58, 191.14) * mm});
            skFitSpline(sketch, "E364", {"points": [v(-159.58, 191.14) * mm, v(-160.65, 186.74) * mm, v(-161.66, 182.65) * mm, v(-161.8, 182.04) * mm]});
            skFitSpline(sketch, "E365", {"points": [v(-161.8, 182.04) * mm, v(-162.04, 181.1) * mm, v(-160.6, 180.89) * mm, v(-152.8, 180.7) * mm]});
            skFitSpline(sketch, "E366", {"points": [v(-152.8, 180.7) * mm, v(-146.97, 180.58) * mm, v(-143.35, 180.2) * mm, v(-143.02, 179.66) * mm]});
            skFitSpline(sketch, "E367", {"points": [v(-143.02, 179.66) * mm, v(-142.41, 178.68) * mm, v(-144.07, 172.79) * mm, v(-145.4, 171.17) * mm]});
            skFitSpline(sketch, "E368", {"points": [v(-145.4, 171.17) * mm, v(-146.2, 170.23) * mm, v(-147.83, 170.13) * mm, v(-155.74, 170.56) * mm]});
            skLineSegment(sketch, "E369", {"start": v(-155.74, 170.56) * mm, "end": v(-165.13, 171.07) * mm});
            skLineSegment(sketch, "E370", {"start": v(-165.13, 171.07) * mm, "end": v(-166.72, 164.47) * mm});
            skFitSpline(sketch, "E371", {"points": [v(-166.72, 164.47) * mm, v(-168.53, 156.92) * mm, v(-169.62, 150.4) * mm, v(-170.3, 143.15) * mm]});
            skFitSpline(sketch, "E372", {"points": [v(-170.3, 143.15) * mm, v(-170.69, 138.84) * mm, v(-171.03, 137.92) * mm, v(-172.64, 136.87) * mm]});
            skFitSpline(sketch, "E373", {"points": [v(-172.64, 136.87) * mm, v(-175.08, 135.27) * mm, v(-182.56, 134.7) * mm, v(-183.84, 136) * mm]});
            skFitSpline(sketch, "E374", {"points": [v(126.9, 136.58) * mm, v(121.05, 138.46) * mm, v(115.7, 143.46) * mm, v(114.21, 148.4) * mm]});
            skFitSpline(sketch, "E375", {"points": [v(114.21, 148.4) * mm, v(112.76, 153.26) * mm, v(113.59, 163.12) * mm, v(115.87, 168.03) * mm]});
            skFitSpline(sketch, "E376", {"points": [v(115.87, 168.03) * mm, v(119.6, 176.03) * mm, v(126.32, 181.7) * mm, v(134.25, 183.54) * mm]});
            skFitSpline(sketch, "E377", {"points": [v(134.25, 183.54) * mm, v(141.52, 185.22) * mm, v(151.26, 183.23) * mm, v(154.42, 179.43) * mm]});
            skFitSpline(sketch, "E378", {"points": [v(154.42, 179.43) * mm, v(155.9, 177.65) * mm, v(154.6, 177.1) * mm, v(147.83, 176.64) * mm]});
            skFitSpline(sketch, "E379", {"points": [v(147.83, 176.64) * mm, v(144.69, 176.43) * mm, v(140.93, 175.75) * mm, v(139.47, 175.14) * mm]});
            skFitSpline(sketch, "E380", {"points": [v(139.47, 175.14) * mm, v(132.67, 172.3) * mm, v(128.2, 165.5) * mm, v(128.1, 157.86) * mm]});
            skFitSpline(sketch, "E381", {"points": [v(128.1, 157.86) * mm, v(127.97, 148.8) * mm, v(133.7, 144.61) * mm, v(142.75, 147.13) * mm]});
            skLineSegment(sketch, "E382", {"start": v(142.75, 147.13) * mm, "end": v(145.58, 147.91) * mm});
            skLineSegment(sketch, "E383", {"start": v(145.58, 147.91) * mm, "end": v(143.02, 150.75) * mm});
            skFitSpline(sketch, "E384", {"points": [v(143.02, 150.75) * mm, v(134.47, 160.22) * mm, v(139.5, 174.6) * mm, v(151.37, 174.6) * mm]});
            skFitSpline(sketch, "E385", {"points": [v(151.37, 174.6) * mm, v(155.58, 174.6) * mm, v(157.91, 173.5) * mm, v(159.66, 170.71) * mm]});
            skFitSpline(sketch, "E386", {"points": [v(159.66, 170.71) * mm, v(160.95, 168.66) * mm, v(161.14, 167.4) * mm, v(160.87, 162.7) * mm]});
            skFitSpline(sketch, "E387", {"points": [v(160.87, 162.7) * mm, v(160.69, 159.63) * mm, v(160.3, 156.36) * mm, v(160, 155.44) * mm]});
            skFitSpline(sketch, "E388", {"points": [v(160, 155.44) * mm, v(159.32, 153.37) * mm, v(160.82, 153.21) * mm, v(164.31, 154.97) * mm]});
            skFitSpline(sketch, "E389", {"points": [v(164.31, 154.97) * mm, v(168.41, 157.05) * mm, v(170.04, 159) * mm, v(170.07, 161.9) * mm]});
            skFitSpline(sketch, "E390", {"points": [v(170.07, 161.9) * mm, v(170.08, 163.36) * mm, v(170.53, 166.81) * mm, v(171.06, 169.57) * mm]});
            skFitSpline(sketch, "E391", {"points": [v(171.06, 169.57) * mm, v(171.6, 172.33) * mm, v(171.86, 174.76) * mm, v(171.66, 174.96) * mm]});
            skFitSpline(sketch, "E392", {"points": [v(171.66, 174.96) * mm, v(171.45, 175.17) * mm, v(170.12, 175.34) * mm, v(168.72, 175.34) * mm]});
            skFitSpline(sketch, "E393", {"points": [v(168.72, 175.34) * mm, v(166.17, 175.34) * mm, v(166.16, 175.36) * mm, v(166.66, 178.04) * mm]});
            skFitSpline(sketch, "E394", {"points": [v(166.66, 178.04) * mm, v(167.46, 182.3) * mm, v(168.56, 183.52) * mm, v(171.6, 183.52) * mm]});
            skFitSpline(sketch, "E395", {"points": [v(171.6, 183.52) * mm, v(174.2, 183.52) * mm, v(174.36, 183.67) * mm, v(175.88, 187.8) * mm]});
            skFitSpline(sketch, "E396", {"points": [v(175.88, 187.8) * mm, v(180.22, 199.6) * mm, v(185.9, 202.36) * mm, v(189.42, 194.38) * mm]});
            skLineSegment(sketch, "E397", {"start": v(189.42, 194.38) * mm, "end": v(190.87, 191.12) * mm});
            skLineSegment(sketch, "E398", {"start": v(190.87, 191.12) * mm, "end": v(189.02, 187.88) * mm});
            skFitSpline(sketch, "E399", {"points": [v(189.02, 187.88) * mm, v(188, 186.1) * mm, v(187.16, 184.39) * mm, v(187.15, 184.08) * mm]});
            skFitSpline(sketch, "E400", {"points": [v(187.15, 184.08) * mm, v(187.15, 183.77) * mm, v(189.49, 183.52) * mm, v(192.35, 183.52) * mm]});
            skFitSpline(sketch, "E401", {"points": [v(192.35, 183.52) * mm, v(197.32, 183.52) * mm, v(197.56, 183.44) * mm, v(197.56, 181.77) * mm]});
            skFitSpline(sketch, "E402", {"points": [v(197.56, 181.77) * mm, v(197.56, 180.81) * mm, v(197.2, 178.97) * mm, v(196.74, 177.68) * mm]});
            skFitSpline(sketch, "E403", {"points": [v(196.74, 177.68) * mm, v(195.93, 175.35) * mm, v(195.92, 175.34) * mm, v(190.5, 175.34) * mm]});
            skFitSpline(sketch, "E404", {"points": [v(190.5, 175.34) * mm, v(186.52, 175.34) * mm, v(184.97, 175.06) * mm, v(184.67, 174.3) * mm]});
            skFitSpline(sketch, "E405", {"points": [v(184.67, 174.3) * mm, v(184.45, 173.72) * mm, v(183.86, 169.28) * mm, v(183.36, 164.44) * mm]});
            skFitSpline(sketch, "E406", {"points": [v(183.36, 164.44) * mm, v(182.36, 154.73) * mm, v(182.85, 148.74) * mm, v(184.7, 148.02) * mm]});
            skFitSpline(sketch, "E407", {"points": [v(184.7, 148.02) * mm, v(186.5, 147.34) * mm, v(192.17, 150.68) * mm, v(197.26, 155.44) * mm]});
            skFitSpline(sketch, "E408", {"points": [v(197.26, 155.44) * mm, v(199.78, 157.8) * mm, v(202.18, 159.72) * mm, v(202.6, 159.72) * mm]});
            skFitSpline(sketch, "E409", {"points": [v(202.6, 159.72) * mm, v(203.93, 159.72) * mm, v(204.3, 156.15) * mm, v(203.27, 153.17) * mm]});
            skFitSpline(sketch, "E410", {"points": [v(203.27, 153.17) * mm, v(200, 143.67) * mm, v(185.58, 134.51) * mm, v(177.34, 136.7) * mm]});
            skFitSpline(sketch, "E411", {"points": [v(177.34, 136.7) * mm, v(174.42, 137.49) * mm, v(172.08, 140.4) * mm, v(171.1, 144.47) * mm]});
            skFitSpline(sketch, "E412", {"points": [v(171.1, 144.47) * mm, v(170.29, 147.9) * mm, v(170.1, 147.99) * mm, v(167.19, 146.17) * mm]});
            skFitSpline(sketch, "E413", {"points": [v(167.19, 146.17) * mm, v(164.96, 144.78) * mm, v(163.48, 144.49) * mm, v(159.04, 144.55) * mm]});
            skFitSpline(sketch, "E414", {"points": [v(159.04, 144.55) * mm, v(153.88, 144.62) * mm, v(153.5, 144.5) * mm, v(150.9, 142.12) * mm]});
            skFitSpline(sketch, "E415", {"points": [v(150.9, 142.12) * mm, v(146.2, 137.83) * mm, v(142.2, 136.32) * mm, v(135.08, 136.14) * mm]});
            skFitSpline(sketch, "E416", {"points": [v(135.08, 136.14) * mm, v(131.6, 136.05) * mm, v(127.92, 136.25) * mm, v(126.9, 136.58) * mm]});
            skFitSpline(sketch, "E417", {"points": [v(154.17, 161.8) * mm, v(154.55, 165) * mm, v(154.4, 165.72) * mm, v(153.35, 166.13) * mm]});
            skFitSpline(sketch, "E418", {"points": [v(153.35, 166.13) * mm, v(151.52, 166.83) * mm, v(150.44, 165.37) * mm, v(150.55, 162.34) * mm]});
            skFitSpline(sketch, "E419", {"points": [v(150.55, 162.34) * mm, v(150.68, 159.12) * mm, v(152.04, 156.3) * mm, v(153.02, 157.28) * mm]});
            skFitSpline(sketch, "E420", {"points": [v(153.02, 157.28) * mm, v(153.4, 157.66) * mm, v(153.92, 159.7) * mm, v(154.17, 161.8) * mm]});
            skFitSpline(sketch, "E421", {"points": [v(-216, 222.42) * mm, v(-220.54, 224.72) * mm, v(-220.51, 230.49) * mm, v(-215.96, 232.8) * mm]});
            skFitSpline(sketch, "E422", {"points": [v(-215.96, 232.8) * mm, v(-213.66, 233.97) * mm, v(-210.56, 234.1) * mm, v(-184.95, 234.1) * mm]});
            skLineSegment(sketch, "E423", {"start": v(-184.95, 234.1) * mm, "end": v(-156.5, 234.1) * mm});
            skLineSegment(sketch, "E424", {"start": v(-156.5, 234.1) * mm, "end": v(-156.5, 236.32) * mm});
            skFitSpline(sketch, "E425", {"points": [v(-156.5, 236.32) * mm, v(-156.5, 240) * mm, v(-154.3, 244.46) * mm, v(-151.87, 245.72) * mm]});
            skFitSpline(sketch, "E426", {"points": [v(-151.87, 245.72) * mm, v(-149.38, 247) * mm, v(-4.22, 272.04) * mm, v(0.76, 272.04) * mm]});
            skFitSpline(sketch, "E427", {"points": [v(0.76, 272.04) * mm, v(4.02, 272.04) * mm, v(145.06, 248.14) * mm, v(150.09, 246.74) * mm]});
            skFitSpline(sketch, "E428", {"points": [v(150.09, 246.74) * mm, v(153.86, 245.69) * mm, v(156.5, 242.32) * mm, v(157.1, 237.8) * mm]});
            skLineSegment(sketch, "E429", {"start": v(157.1, 237.8) * mm, "end": v(157.58, 234.1) * mm});
            skLineSegment(sketch, "E430", {"start": v(157.58, 234.1) * mm, "end": v(185.64, 234.1) * mm});
            skFitSpline(sketch, "E431", {"points": [v(185.64, 234.1) * mm, v(214.56, 234.1) * mm, v(217.69, 233.82) * mm, v(219.15, 231.1) * mm]});
            skFitSpline(sketch, "E432", {"points": [v(219.15, 231.1) * mm, v(220.3, 228.93) * mm, v(220, 225.49) * mm, v(218.45, 223.59) * mm]});
            skLineSegment(sketch, "E433", {"start": v(218.45, 223.59) * mm, "end": v(217.03, 221.83) * mm});
            skLineSegment(sketch, "E434", {"start": v(217.03, 221.83) * mm, "end": v(1.44, 221.65) * mm});
            skFitSpline(sketch, "E435", {"points": [v(1.44, 221.65) * mm, v(-171.4, 221.51) * mm, v(-214.51, 221.66) * mm, v(-216, 222.42) * mm]});
            skLineSegment(sketch, "E436", {"start": v(-216, -140.24) * mm, "end": v(-216, -140.24) * mm});
            skSolve(sketch);
        }
        {
            var Q0;
            Q0=qSketchRegion(id+"F7",true);
            extrude(context, id + "F8", {"entities" : qUnion([Q0]), "operationType" : NewBodyOperationType.REMOVE, "oppositeDirection" : true, "depth" : 2 * mm});
        }
        {
            var Q0;
            Q0=makeQuery(id+"F3.opExtrude","SWEPT_FACE",FACE,{"disambiguationData":[OSD([sQuery(id+"F2.wireOp",EDGE,"E1.top")])]});
            var sketch = newSketch(context, id + "F9", { "sketchPlane" : qUnion([Q0])});
            skLineSegment(sketch, "E437.bottom", {"start": v(710, -700) * mm, "end": v(620, -700) * mm});
            skLineSegment(sketch, "E437.top", {"start": v(710, -610) * mm, "end": v(620, -610) * mm});
            skLineSegment(sketch, "E437.left", {"start": v(710, -700) * mm, "end": v(710, -610) * mm});
            skLineSegment(sketch, "E437.right", {"start": v(620, -700) * mm, "end": v(620, -610) * mm});
            skSolve(sketch);
        }
        {
            var Q0;
            Q0=makeQuery(id+"F9.imprint","IMPRINT",FACE,{"disambiguationData":[TD([[makeQuery(id+"F9.imprint","IMPRINT",EDGE,{"derivedFrom":sQuery(id+"F9.wireOp",EDGE,"E437.bottom")}),-1.0]])]});
            extrude(context, id + "F10", {"entities" : qUnion([Q0]), "oppositeDirection" : true, "depth" : 400 * mm});
        }
        {
            var Q0;
            Q0=makeQuery(id+"F10.opExtrude","SWEPT_FACE",FACE,{"disambiguationData":[OSD([sQuery(id+"F9.wireOp",EDGE,"E437.right")])]});
            var sketch = newSketch(context, id + "F11", { "sketchPlane" : qUnion([Q0])});
            skLineSegment(sketch, "E438.bottom", {"start": v(700, -100) * mm, "end": v(-700, -100) * mm});
            skLineSegment(sketch, "E438.top", {"start": v(700, 0) * mm, "end": v(-700, 0) * mm});
            skLineSegment(sketch, "E438.left", {"start": v(700, -100) * mm, "end": v(700, 0) * mm});
            skLineSegment(sketch, "E438.right", {"start": v(-700, -100) * mm, "end": v(-700, 0) * mm});
            skSolve(sketch);
        }
        {
            var Q0;
            {var subQ3=sQuery(id+"F11.wireOp",EDGE,"E438.right");Q0=makeQuery(id+"F11.imprint","IMPRINT",FACE,{"disambiguationData":[TD([[makeQuery(id+"F11.imprint","IMPRINT",EDGE,{"derivedFrom":subQ3}),-1.0]])]});}
            var Q1;
            {var subQ0=sQuery(id+"F11.wireOp",EDGE,"E438.left");Q1=makeQuery(id+"F11.imprint","IMPRINT",FACE,{"disambiguationData":[TD([[makeQuery(id+"F11.imprint","IMPRINT",EDGE,{"derivedFrom":subQ0}),1.0]])]});}
            extrude(context, id + "F12", {"entities" : qUnion([Q0, Q1]), "depth" : 40 * mm});
        }
    });
